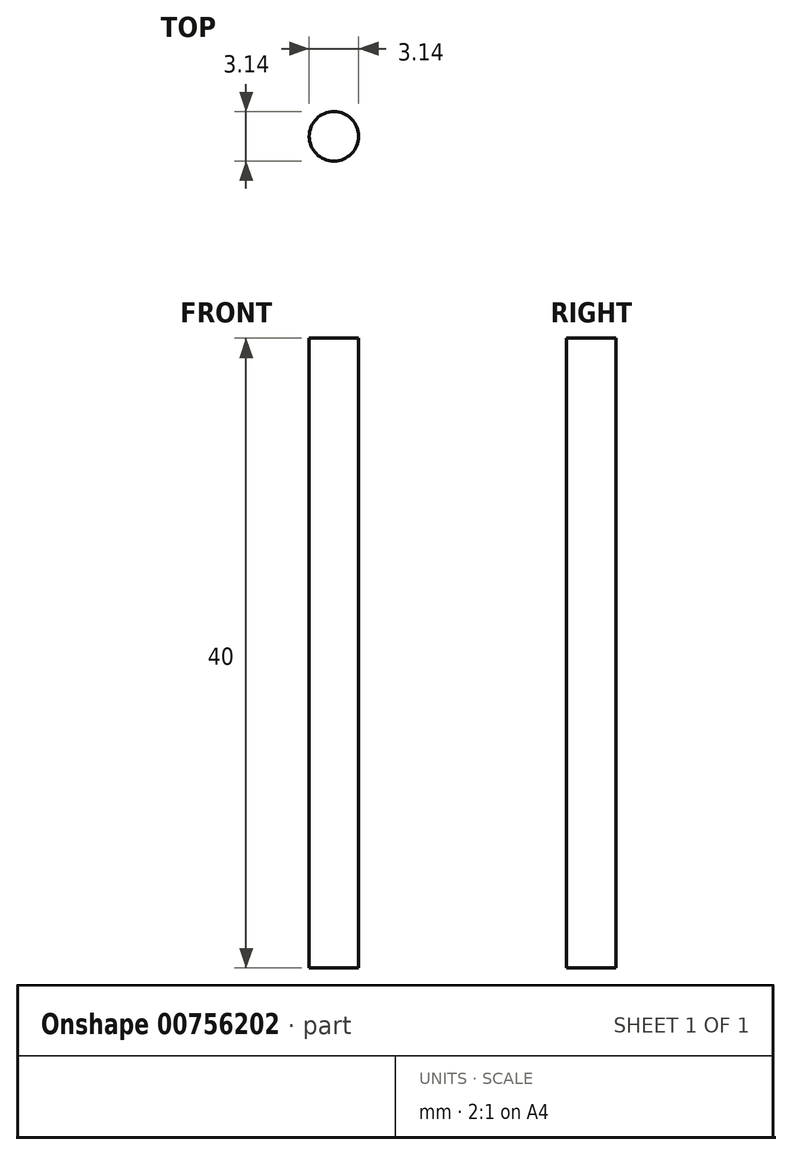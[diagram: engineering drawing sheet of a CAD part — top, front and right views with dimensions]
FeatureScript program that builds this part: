
annotation { "Feature Type Name" : "Feature", "Feature Type Description" : "" }
export const myFeature = defineFeature(function(context is Context, id is Id, definition is map)
    precondition{}
    {
        {
            var Q0;
            Q0=qCreatedBy(makeId("Top.planeOp"),FACE);
            var sketch = newSketch(context, id + "F0", { "sketchPlane" : qUnion([Q0])});
            skCircle(sketch, "E0", {"center": v(0, 0) * mm, "radius": 1.57 * mm});
            skSolve(sketch);
        }
        {
            var Q0;
            Q0 = qSketchRegion(id + "F0", true);
            extrude(context, id + "F1", {"entities" : qUnion([Q0]), "endBound" : BoundingType.SYMMETRIC, "depth" : 40 * mm, "offsetDistance" : 25 * mm});
        }
    });
